# Revit family: Shower_Arm-DXV-Square-D3570042X_Series
name_source: partatom
category: Plumbing Fixtures
units: mm (PartAtom-declared; Revit-internal decimal feet)

## family parameters
Cut with Voids When Loaded = No
Host = Face
OmniClass Number = 23.45.05.14.17
OmniClass Title = Showers
Part Type = Normal
Room Calculation Point = No
Round Connector Dimension = Use Diameter
Shared = Yes

## types (2) — shared parameters
Assembly Code = D2090800
CW Connection = No
CWFU = 3
Default Elevation = 78"
Finish = Brass-DXV-100-Polished Chrome
HW Connection = No
HWFU = 3
Installation Type = Wall Mounted
Manufacturer = DXV
Material = Brass-DXV-100-Polished Chrome
Model = D35700426.100
Price = Prices may vary. Please consult Manufacturer Representative for most up-to-date price list.
Product Documentation Link = https://dxv01.blob.core.windows.net
Product Page URL = https://www.dxv.com
Tempered Connection Diameter = 1/2"
Tempered Water Connection = Yes
URL = https://www.dxv.com
Vent Connection = No
WFU = 4
Waste Connection = No
Width = 2 3/8"

## per-type parameters (varying)
| type | Description | Height | Outlet Diameter |
| D35700426.100 | SLIM SQUARE 16 INCH SHOWER ARM | 15 3/4" | 1/2" |
| D35700420.100 | SLIM SQUARE 20 INCH SHOWER ARM | 19 11/16" | 24" |

## geometry (parser evidence)
native form markers: Sweep x3
no freeform markers — native parametric forms only
